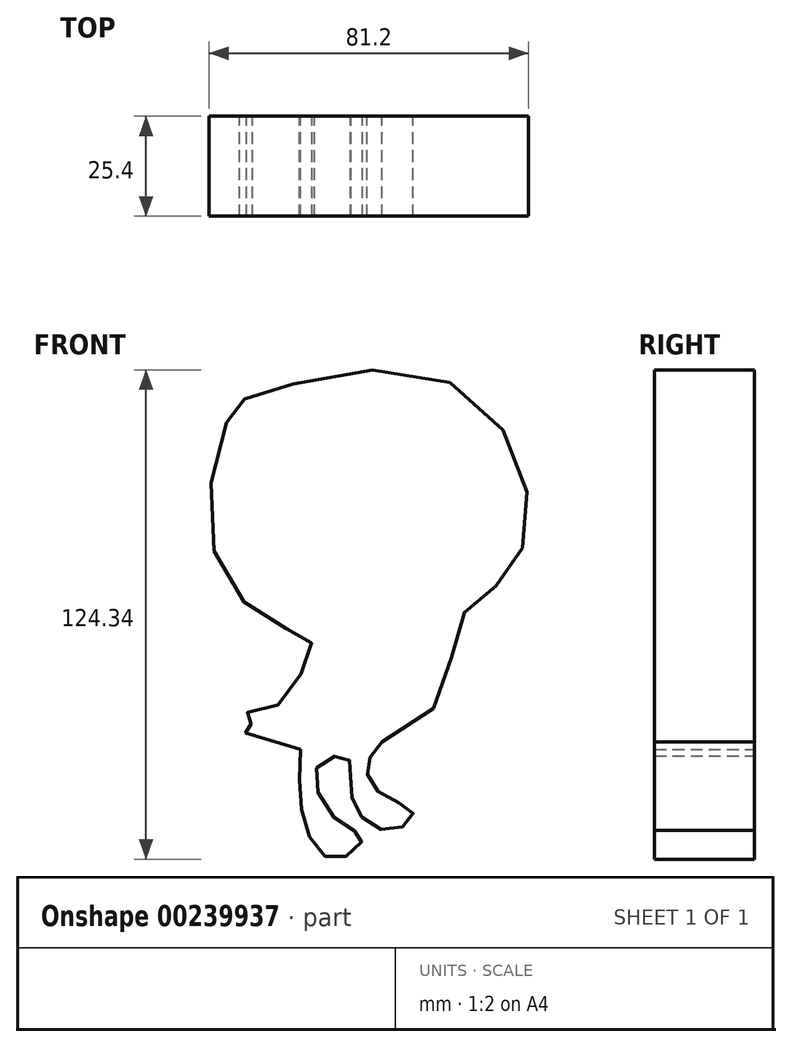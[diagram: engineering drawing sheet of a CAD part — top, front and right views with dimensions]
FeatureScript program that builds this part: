
annotation { "Feature Type Name" : "Feature", "Feature Type Description" : "" }
export const myFeature = defineFeature(function(context is Context, id is Id, definition is map)
    precondition{}
    {
        {
            var Q0;
            Q0=qCreatedBy(makeId("Front.planeOp"),FACE);
            var sketch = newSketch(context, id + "F0", { "sketchPlane" : qUnion([Q0])});
            skFitSpline(sketch, "E0", {"points": [v(-32.96, 48.5) * mm, v(-37.94, 45.14) * mm, v(-43.64, 14.14) * mm, v(-28.59, -8.66) * mm, v(-18.13, -13.44) * mm, v(-19.85, -20.6) * mm, v(-27.68, -30.51) * mm, v(-34.37, -32.14) * mm, v(-32.93, -34.4) * mm, v(-32.93, -34.65) * mm, v(-36.03, -35.38) * mm, v(-18.52, -41.41) * mm, v(13.94, -29.47) * mm, v(20.1, -7.77) * mm, v(31.06, 2.37) * mm, v(36.87, 24.3) * mm, v(12.3, 53.88) * mm, v(-32.96, 48.5) * mm]});
            skFitSpline(sketch, "E1", {"points": [v(-20.64, -41.17) * mm, v(-19.63, -60.16) * mm, v(-11.72, -69.09) * mm, v(-4.99, -63.96) * mm, v(-11.14, -59.42) * mm, v(-16.56, -45.8) * mm, v(-9.09, -43.17) * mm, v(-7.92, -47.42) * mm, v(-6.3, -56.79) * mm, v(2.63, -61.77) * mm, v(7.9, -57.37) * mm, v(0, -52.69) * mm, v(-3.82, -45.66) * mm, v(0, -39.26) * mm], "startDerivative": vector(-11, -178.39) * mm, "endDerivative": vector(77.52, 88.42) * mm});
            skSolve(sketch);
        }
        {
            var Q0;
            Q0 = qSketchRegion(id + "F0", true);
            extrude(context, id + "F1", {"entities" : qUnion([Q0]), "depth" : 25.4 * mm});
        }
    });
